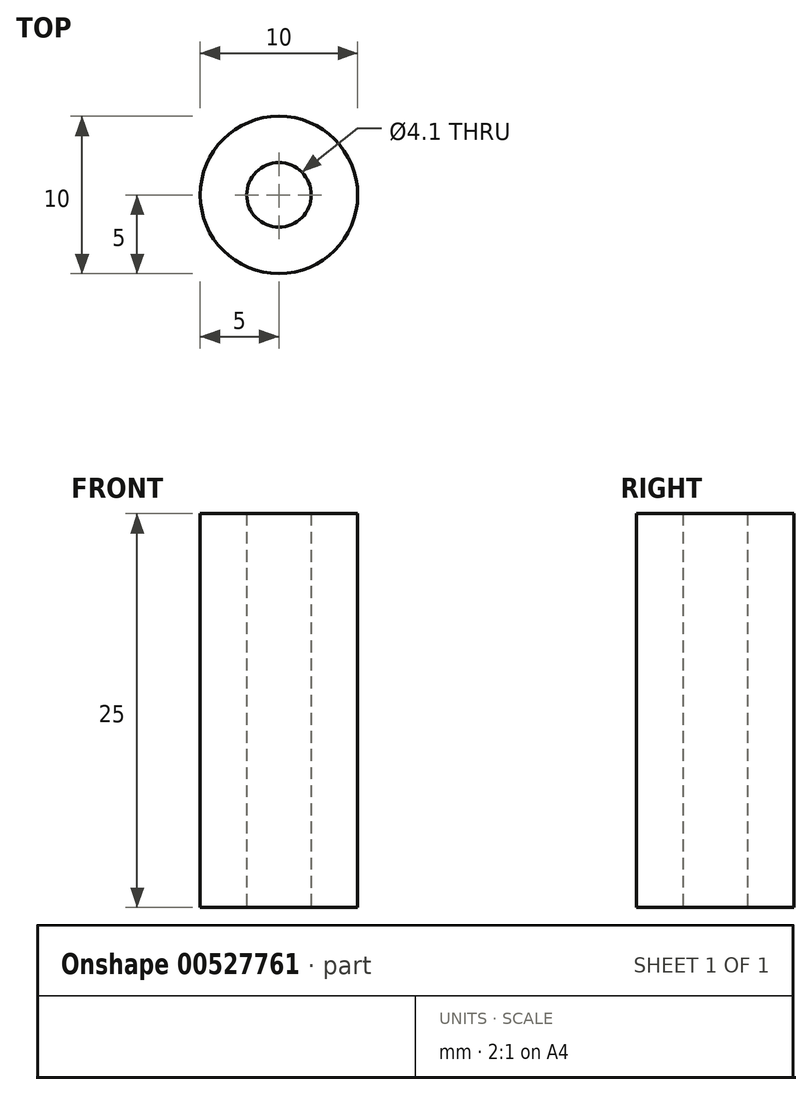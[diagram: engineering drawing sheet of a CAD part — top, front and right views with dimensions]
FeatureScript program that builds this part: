
annotation { "Feature Type Name" : "Feature", "Feature Type Description" : "" }
export const myFeature = defineFeature(function(context is Context, id is Id, definition is map)
    precondition{}
    {
        {
            var Q0;
            Q0=qCreatedBy(makeId("Top.planeOp"),FACE);
            var sketch = newSketch(context, id + "F0", { "sketchPlane" : qUnion([Q0])});
            skCircle(sketch, "E0", {"center": v(0, 0) * mm, "radius": 5 * mm});
            skCircle(sketch, "E1", {"center": v(0, 0) * mm, "radius": 2.05 * mm});
            skSolve(sketch);
        }
        {
            var Q0;
            Q0 = qSketchRegion(id + "F0", true);
            extrude(context, id + "F1", {"entities" : qUnion([Q0]), "depth" : 25 * mm, "offsetDistance" : 25 * mm});
        }
    });
